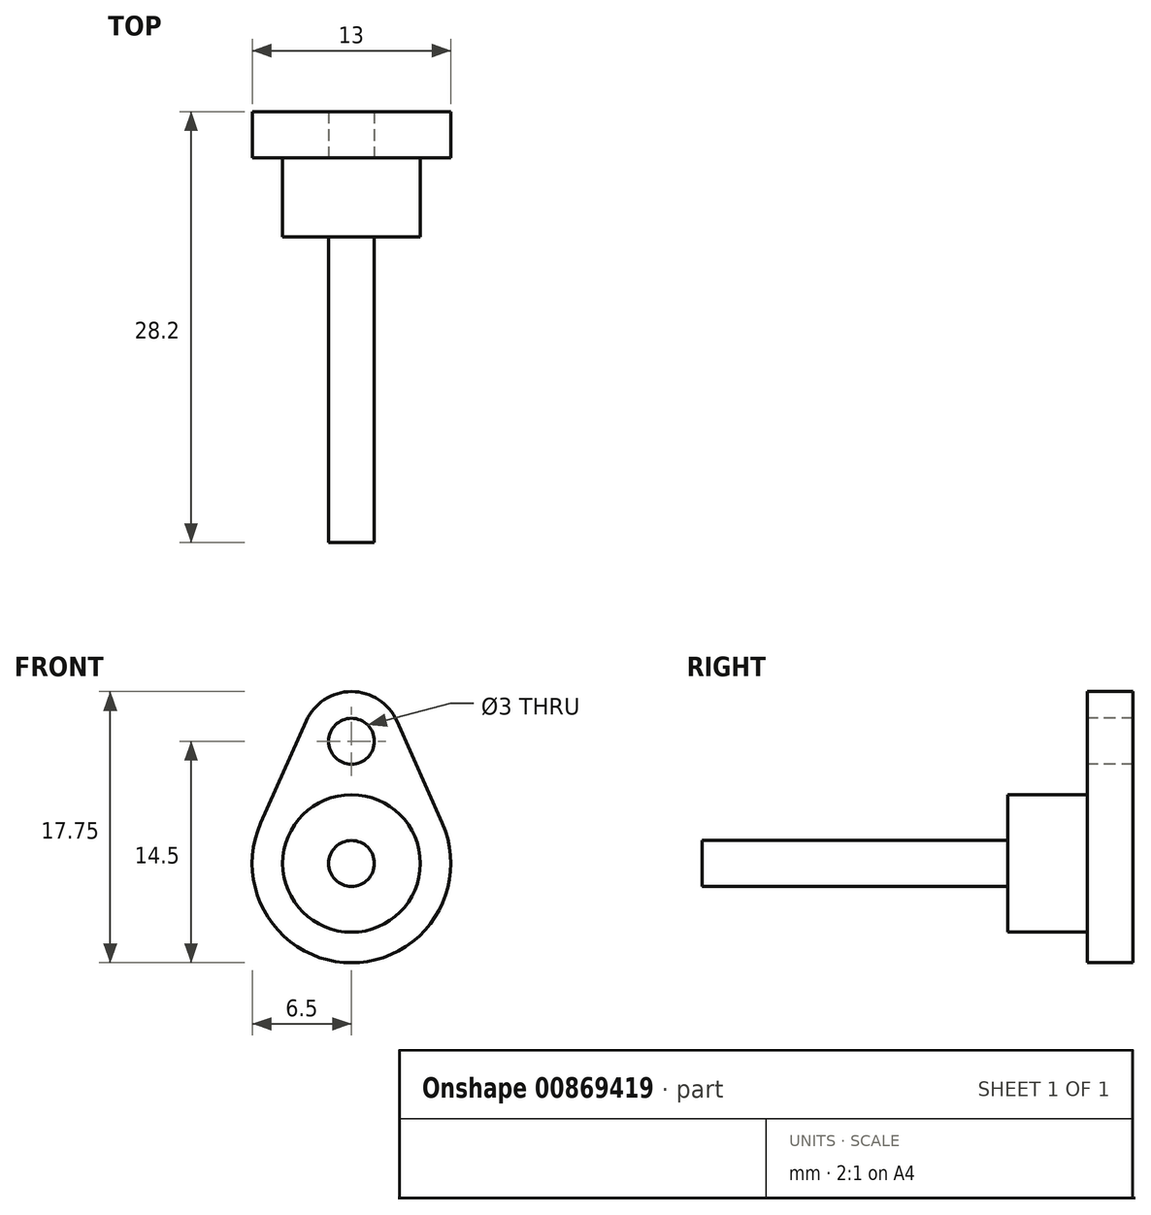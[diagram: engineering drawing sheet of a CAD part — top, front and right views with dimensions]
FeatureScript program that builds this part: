
annotation { "Feature Type Name" : "Feature", "Feature Type Description" : "" }
export const myFeature = defineFeature(function(context is Context, id is Id, definition is map)
    precondition{}
    {
        {
            var Q0;
            Q0=qCreatedBy(makeId("Front.planeOp"),FACE);
            var sketch = newSketch(context, id + "F0", { "sketchPlane" : qUnion([Q0])});
            skArc(sketch, "E0", {"start": v(2.97, 9.32) * mm, "mid": v(0, 11.25) * mm, "end": v(-2.97, 9.32) * mm});
            skCircle(sketch, "E1", {"center": v(0, 0) * mm, "radius": 1.5 * mm, "construction": true});
            skArc(sketch, "E2", {"start": v(-5.94, 2.64) * mm, "mid": v(0, -6.5) * mm, "end": v(5.94, 2.64) * mm});
            skLineSegment(sketch, "E3", {"start": v(-2.97, 9.32) * mm, "end": v(-5.94, 2.64) * mm});
            skLineSegment(sketch, "E4", {"start": v(2.97, 9.32) * mm, "end": v(5.94, 2.64) * mm});
            skCircle(sketch, "E5", {"center": v(0, 8) * mm, "radius": 1.5 * mm});
            skSolve(sketch);
        }
        {
            var Q0;
            Q0=makeQuery(id+"F0.imprint","IMPRINT",FACE,{"disambiguationData":[TD([[makeQuery(id+"F0.imprint","IMPRINT",EDGE,{"derivedFrom":sQuery(id+"F0.wireOp",EDGE,"E0")}),1.0]])]});
            extrude(context, id + "F1", {"entities" : qUnion([Q0]), "oppositeDirection" : true, "depth" : 3 * mm, "offsetDistance" : 25 * mm});
        }
        {
            var Q0;
            Q0=makeQuery(id+"F1.opExtrude","CAP_FACE",FACE,{"disambiguationData":[OSD([sQuery(id+"F0.wireOp",EDGE,"E0"),sQuery(id+"F0.wireOp",EDGE,"E2"),sQuery(id+"F0.wireOp",EDGE,"E3"),sQuery(id+"F0.wireOp",EDGE,"E4"),sQuery(id+"F0.wireOp",EDGE,"E5")])],"isStart":true});
            var sketch = newSketch(context, id + "F2", { "sketchPlane" : qUnion([Q0])});
            skCircle(sketch, "E6", {"center": v(0, 0) * mm, "radius": 4.5 * mm});
            skSolve(sketch);
        }
        {
            var Q0;
            Q0=makeQuery(id+"F2.imprint","IMPRINT",FACE,{"disambiguationData":[TD([[makeQuery(id+"F2.imprint","IMPRINT",EDGE,{"derivedFrom":sQuery(id+"F2.wireOp",EDGE,"E6")}),1.0]])]});
            extrude(context, id + "F3", {"entities" : qUnion([Q0]), "operationType" : NewBodyOperationType.ADD, "depth" : 5.2 * mm, "offsetDistance" : 25 * mm});
        }
        {
            var Q0;
            Q0=makeQuery(id+"F3.opExtrude","CAP_FACE",FACE,{"disambiguationData":[OSD([sQuery(id+"F2.wireOp",EDGE,"E6")])],"isStart":false});
            var sketch = newSketch(context, id + "F4", { "sketchPlane" : qUnion([Q0])});
            skCircle(sketch, "E7", {"center": v(0, 0) * mm, "radius": 1.5 * mm});
            skSolve(sketch);
        }
        {
            var Q0;
            Q0=makeQuery(id+"F4.imprint","IMPRINT",FACE,{"disambiguationData":[TD([[makeQuery(id+"F4.imprint","IMPRINT",EDGE,{"derivedFrom":sQuery(id+"F4.wireOp",EDGE,"E7")}),1.0]])]});
            extrude(context, id + "F5", {"entities" : qUnion([Q0]), "operationType" : NewBodyOperationType.ADD, "depth" : 20 * mm, "offsetDistance" : 25 * mm});
        }
    });
